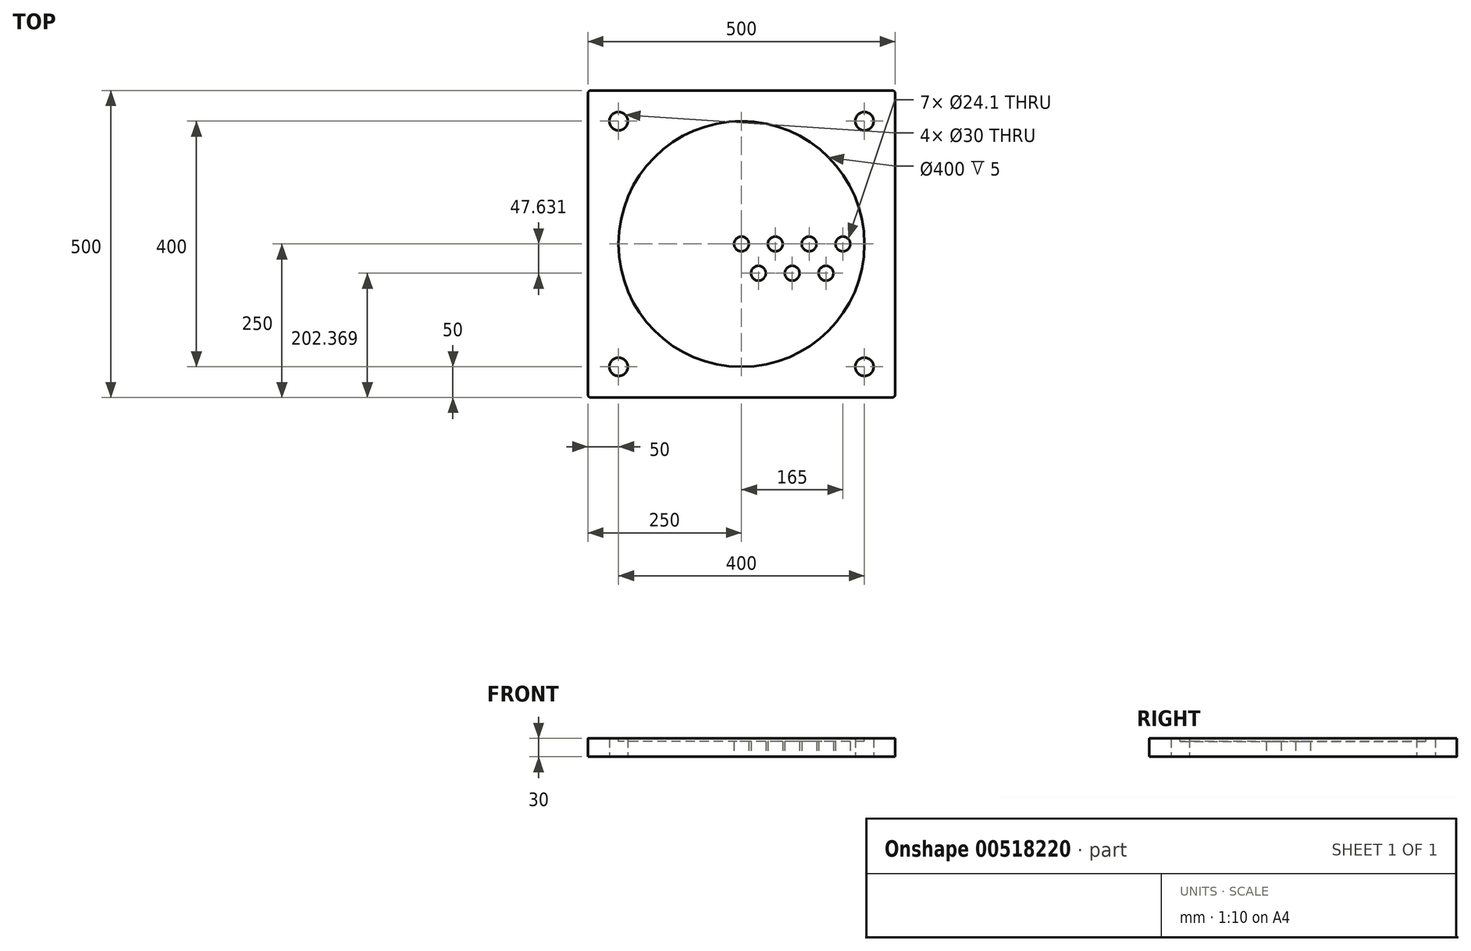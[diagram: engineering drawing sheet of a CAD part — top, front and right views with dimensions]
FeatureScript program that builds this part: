
annotation { "Feature Type Name" : "Feature", "Feature Type Description" : "" }
export const myFeature = defineFeature(function(context is Context, id is Id, definition is map)
    precondition{}
    {
        {
            var Q0;
            Q0=qCreatedBy(makeId("Top.planeOp"),FACE);
            var sketch = newSketch(context, id + "F0", { "sketchPlane" : qUnion([Q0])});
            skLineSegment(sketch, "E0.bottom", {"start": v(250, -250) * mm, "end": v(-250, -250) * mm});
            skLineSegment(sketch, "E0.top", {"start": v(250, 250) * mm, "end": v(-250, 250) * mm});
            skLineSegment(sketch, "E0.left", {"start": v(250, -250) * mm, "end": v(250, 250) * mm});
            skLineSegment(sketch, "E0.right", {"start": v(-250, -250) * mm, "end": v(-250, 250) * mm});
            skPoint(sketch, "E0.middle", {"position": v(0, 0) * mm});
            skCircle(sketch, "E1", {"center": v(200, 200) * mm, "radius": 15 * mm});
            skCircle(sketch, "E2.MirrorC", {"center": v(-200, 200) * mm, "radius": 15 * mm});
            skCircle(sketch, "E3.MirrorC", {"center": v(-200, -200) * mm, "radius": 15 * mm});
            skCircle(sketch, "E4.MirrorC", {"center": v(200, -200) * mm, "radius": 15 * mm});
            skCircle(sketch, "E5", {"center": v(0, 0) * mm, "radius": 12.05 * mm});
            skCircle(sketch, "E6.1.0.0", {"center": v(55, 0) * mm, "radius": 12.05 * mm});
            skCircle(sketch, "E6.2.0.0", {"center": v(110, 0) * mm, "radius": 12.05 * mm});
            skCircle(sketch, "E6.3.0.0", {"center": v(165, 0) * mm, "radius": 12.05 * mm});
            skLineSegment(sketch, "E6.direction1", {"start": v(0, 0) * mm, "end": v(55, 0) * mm, "construction": true});
            skCircle(sketch, "E7.1.0", {"center": v(27.5, -47.63) * mm, "radius": 12.05 * mm});
            skLineSegment(sketch, "E7.anchor2", {"start": v(0, 0) * mm, "end": v(27.5, -47.63) * mm, "construction": true});
            skCircle(sketch, "E8.1.0.0", {"center": v(82.5, -47.63) * mm, "radius": 12.05 * mm});
            skCircle(sketch, "E8.2.0.0", {"center": v(137.5, -47.63) * mm, "radius": 12.05 * mm});
            skLineSegment(sketch, "E8.direction1", {"start": v(27.5, -47.63) * mm, "end": v(82.5, -47.63) * mm, "construction": true});
            skSolve(sketch);
        }
        {
            var Q0;
            Q0=makeQuery(id+"F0.imprint","IMPRINT",FACE,{"disambiguationData":[TD([[makeQuery(id+"F0.imprint","IMPRINT",EDGE,{"derivedFrom":sQuery(id+"F0.wireOp",EDGE,"E0.bottom")}),-1.0]])]});
            extrude(context, id + "F1", {"entities" : qUnion([Q0]), "depth" : 30 * mm, "offsetDistance" : 25 * mm});
        }
        {
            var Q0;
            Q0=makeQuery(id+"F1.opExtrude","SWEPT_EDGE",EDGE,{"disambiguationData":[OSD([sQuery(id+"F0.wireOp",EDGE,"E0.bottom"),sQuery(id+"F0.wireOp",EDGE,"E0.right")])]});
            var Q1;
            Q1=makeQuery(id+"F1.opExtrude","SWEPT_EDGE",EDGE,{"disambiguationData":[OSD([sQuery(id+"F0.wireOp",EDGE,"E0.bottom"),sQuery(id+"F0.wireOp",EDGE,"E0.left")])]});
            var Q2;
            Q2=makeQuery(id+"F1.opExtrude","SWEPT_EDGE",EDGE,{"disambiguationData":[OSD([sQuery(id+"F0.wireOp",EDGE,"E0.top"),sQuery(id+"F0.wireOp",EDGE,"E0.left")])]});
            var Q3;
            Q3=makeQuery(id+"F1.opExtrude","SWEPT_EDGE",EDGE,{"disambiguationData":[OSD([sQuery(id+"F0.wireOp",EDGE,"E0.top"),sQuery(id+"F0.wireOp",EDGE,"E0.right")])]});
            fillet(context, id + "F2", {"entities" : qUnion([Q0, Q1, Q2, Q3]), "radius" : 5 * mm, "tangentPropagation" : true, "allowEdgeOverflow" : false});
        }
        {
            var Q0;
            Q0=makeQuery(id+"F1.opExtrude","CAP_FACE",FACE,{"disambiguationData":[OSD([sQuery(id+"F0.wireOp",EDGE,"E0.bottom"),sQuery(id+"F0.wireOp",EDGE,"E0.top"),sQuery(id+"F0.wireOp",EDGE,"E0.left"),sQuery(id+"F0.wireOp",EDGE,"E0.right")])],"isStart":false});
            var sketch = newSketch(context, id + "F3", { "sketchPlane" : qUnion([Q0])});
            skCircle(sketch, "E9", {"center": v(0, 0) * mm, "radius": 200 * mm});
            skSolve(sketch);
        }
        {
            var Q0;
            Q0=qSketchRegion(id+"F3",true);
            extrude(context, id + "F4", {"entities" : qUnion([Q0]), "operationType" : NewBodyOperationType.REMOVE, "oppositeDirection" : true, "depth" : 5 * mm, "offsetDistance" : 25 * mm});
        }
    });
